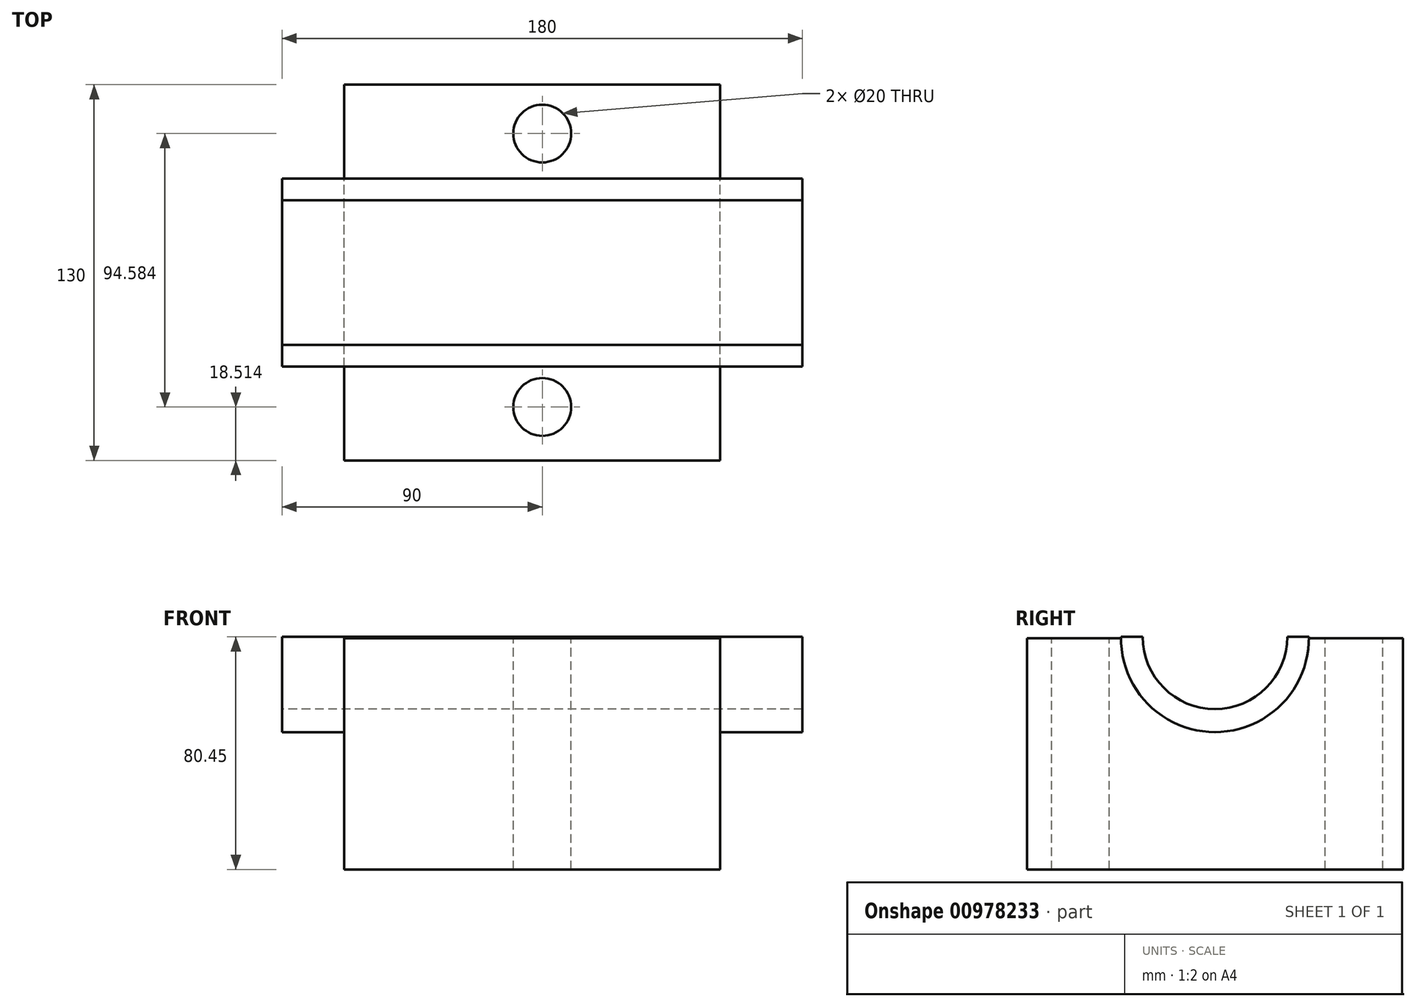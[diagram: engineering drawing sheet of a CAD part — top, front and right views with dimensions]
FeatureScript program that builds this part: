
annotation { "Feature Type Name" : "Feature", "Feature Type Description" : "" }
export const myFeature = defineFeature(function(context is Context, id is Id, definition is map)
    precondition{}
    {
        {
            var Q0;
            Q0=qCreatedBy(makeId("Front.planeOp"),FACE);
            var sketch = newSketch(context, id + "F0", { "sketchPlane" : qUnion([Q0])});
            skLineSegment(sketch, "E0.bottom", {"start": v(-68.54, 39.45) * mm, "end": v(61.46, 39.45) * mm});
            skLineSegment(sketch, "E0.top", {"start": v(-68.54, -40.55) * mm, "end": v(61.46, -40.55) * mm});
            skLineSegment(sketch, "E0.left", {"start": v(-68.54, 39.45) * mm, "end": v(-68.54, -40.55) * mm});
            skLineSegment(sketch, "E0.right", {"start": v(61.46, 39.45) * mm, "end": v(61.46, -40.55) * mm});
            skSolve(sketch);
        }
        {
            var Q0;
            Q0=makeQuery(id+"F0.imprint","IMPRINT",FACE,{"disambiguationData":[TD([[makeQuery(id+"F0.imprint","IMPRINT",EDGE,{"derivedFrom":sQuery(id+"F0.wireOp",EDGE,"E0.bottom")}),-1.0]])]});
            extrude(context, id + "F1", {"entities" : qUnion([Q0]), "depth" : 65 * mm, "offsetDistance" : 25 * mm});
        }
        {
            var Q0;
            Q0=makeQuery(id+"F1.opExtrude","SWEPT_BODY",BODY,{"disambiguationData":[OSD([sQuery(id+"F0.wireOp",EDGE,"E0.bottom"),sQuery(id+"F0.wireOp",EDGE,"E0.top"),sQuery(id+"F0.wireOp",EDGE,"E0.left"),sQuery(id+"F0.wireOp",EDGE,"E0.right")])]});
            var Q1;
            Q1=makeQuery(id+"F1.opExtrude","CAP_FACE",FACE,{"disambiguationData":[OSD([sQuery(id+"F0.wireOp",EDGE,"E0.bottom"),sQuery(id+"F0.wireOp",EDGE,"E0.top"),sQuery(id+"F0.wireOp",EDGE,"E0.left"),sQuery(id+"F0.wireOp",EDGE,"E0.right")])],"isStart":true});
            mirror(context, id + "F2", {"operationType" : NewBodyOperationType.ADD, "entities" : qUnion([Q0]), "mirrorPlane" : qUnion([Q1])});
        }
        {
            var Q0;
            Q0=qCreatedBy(makeId("Right.planeOp"),FACE);
            var sketch = newSketch(context, id + "F3", { "sketchPlane" : qUnion([Q0])});
            skArc(sketch, "E1", {"start": v(-32.49, 39.9) * mm, "mid": v(0, 6.95) * mm, "end": v(32.49, 39.9) * mm});
            skLineSegment(sketch, "E2", {"start": v(-32.49, 39.9) * mm, "end": v(32.49, 39.9) * mm});
            skSolve(sketch);
        }
        {
            var Q0;
            Q0 = qSketchRegion(id + "F3", true);
            extrude(context, id + "F4", {"entities" : qUnion([Q0]), "operationType" : NewBodyOperationType.ADD, "depth" : 180 * mm, "offsetDistance" : 25 * mm, "symmetric" : true});
        }
        {
            var Q0;
            Q0=makeQuery(id+"F4.opExtrude","CAP_FACE",FACE,{"disambiguationData":[OSD([sQuery(id+"F3.wireOp",EDGE,"E1"),sQuery(id+"F3.wireOp",EDGE,"E2")])],"isStart":true});
            var sketch = newSketch(context, id + "F5", { "sketchPlane" : qUnion([Q0])});
            skPoint(sketch, "E3", {"position": v(0, 39.9) * mm});
            skSolve(sketch);
        }
        {
            var Q0;
            Q0=sQuery(id+"F5.wireOp",VERTEX,"E3");
            var Q1;
            Q1=makeQuery(id+"F1.opExtrude","SWEPT_BODY",BODY,{"disambiguationData":[OSD([sQuery(id+"F0.wireOp",EDGE,"E0.bottom"),sQuery(id+"F0.wireOp",EDGE,"E0.top"),sQuery(id+"F0.wireOp",EDGE,"E0.left"),sQuery(id+"F0.wireOp",EDGE,"E0.right")])]});
            hole(context, id + "F6", {"style" : HoleStyle.SIMPLE, "endStyle" : HoleEndStyle.THROUGH, "holeDiameter" : 50 * mm, "majorDiameter" : 5 * mm, "isTappedThrough" : true, "tappedDepth" : 12 * mm, "tapClearance" : 3, "locations" : qUnion([Q0]), "scope" : qUnion([Q1])});
        }
        {
            var Q0;
            {var subQ0=sQuery(id+"F0.wireOp",EDGE,"E0.left");var subQ2=sQuery(id+"F0.wireOp",EDGE,"E0.right");var subQ4=sQuery(id+"F0.wireOp",EDGE,"E0.bottom");var subQ5=makeQuery(id+"F1.opExtrude","SWEPT_FACE",FACE,{"disambiguationData":[OSD([subQ4])]});Q0=makeQuery(id+"F4.boolean.opBoolean","SPLIT",FACE,{"disambiguationData":[TD([makeQuery(id+"F1.opExtrude","CAP_FACE",FACE,{"disambiguationData":[OSD([subQ4,sQuery(id+"F0.wireOp",EDGE,"E0.top"),subQ0,subQ2])],"isStart":false})])],"derivedFrom":makeQuery(id+"F2.boolean.opBoolean","MERGE",FACE,{"derivedFrom":[subQ5,makeQuery(id+"F2.opPattern","COPY",FACE,{"derivedFrom":subQ5,"instanceName":"1"})]})});}
            var sketch = newSketch(context, id + "F7", { "sketchPlane" : qUnion([Q0])});
            skCircle(sketch, "E4", {"center": v(0, -46.49) * mm, "radius": 10 * mm});
            skSolve(sketch);
        }
        {
            var Q0;
            {var subQ0=sQuery(id+"F0.wireOp",EDGE,"E0.right");var subQ1=sQuery(id+"F0.wireOp",EDGE,"E0.left");var subQ2=sQuery(id+"F0.wireOp",EDGE,"E0.bottom");var subQ5=makeQuery(id+"F1.opExtrude","SWEPT_FACE",FACE,{"disambiguationData":[OSD([subQ2])]});Q0=makeQuery(id+"F4.boolean.opBoolean","SPLIT",FACE,{"disambiguationData":[TD([makeQuery(id+"F2.opPattern","COPY",FACE,{"derivedFrom":makeQuery(id+"F1.opExtrude","CAP_FACE",FACE,{"disambiguationData":[OSD([subQ2,sQuery(id+"F0.wireOp",EDGE,"E0.top"),subQ1,subQ0])],"isStart":false}),"instanceName":"1"})])],"derivedFrom":makeQuery(id+"F2.boolean.opBoolean","MERGE",FACE,{"derivedFrom":[subQ5,makeQuery(id+"F2.opPattern","COPY",FACE,{"derivedFrom":subQ5,"instanceName":"1"})]})});}
            var sketch = newSketch(context, id + "F8", { "sketchPlane" : qUnion([Q0])});
            skCircle(sketch, "E5", {"center": v(0, 48.1) * mm, "radius": 10 * mm});
            skSolve(sketch);
        }
        {
            var Q0;
            Q0=makeQuery(id+"F8.imprint","IMPRINT",FACE,{"disambiguationData":[TD([[makeQuery(id+"F8.imprint","IMPRINT",EDGE,{"derivedFrom":sQuery(id+"F8.wireOp",EDGE,"E5")}),1.0]])]});
            extrude(context, id + "F9", {"entities" : qUnion([Q0]), "operationType" : NewBodyOperationType.REMOVE, "oppositeDirection" : true, "depth" : 100 * mm, "offsetDistance" : 25 * mm});
        }
        {
            var Q0;
            Q0=makeQuery(id+"F7.imprint","IMPRINT",FACE,{"disambiguationData":[TD([[makeQuery(id+"F7.imprint","IMPRINT",EDGE,{"derivedFrom":sQuery(id+"F7.wireOp",EDGE,"E4")}),1.0]])]});
            extrude(context, id + "F10", {"entities" : qUnion([Q0]), "operationType" : NewBodyOperationType.REMOVE, "oppositeDirection" : true, "depth" : 100 * mm, "offsetDistance" : 25 * mm});
        }
    });
